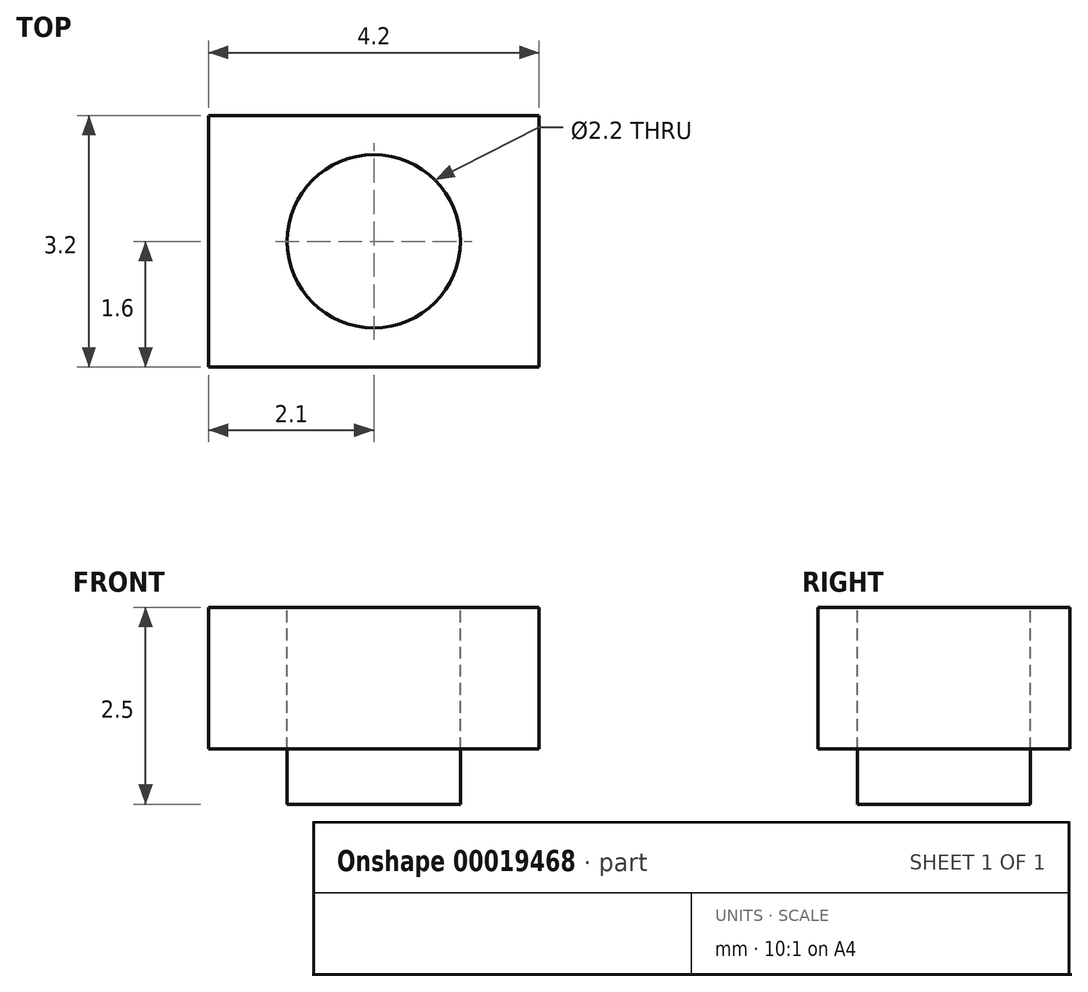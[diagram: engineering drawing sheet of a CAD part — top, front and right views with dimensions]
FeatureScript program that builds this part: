
annotation { "Feature Type Name" : "Feature", "Feature Type Description" : "" }
export const myFeature = defineFeature(function(context is Context, id is Id, definition is map)
    precondition{}
    {
        {
            var Q0;
            Q0=qCreatedBy(makeId("Top.planeOp"),FACE);
            var sketch = newSketch(context, id + "F0", { "sketchPlane" : qUnion([Q0])});
            skLineSegment(sketch, "E0.rect.bottom", {"start": v(2.1, 1.6) * mm, "end": v(-2.1, 1.6) * mm});
            skLineSegment(sketch, "E0.rect.top", {"start": v(2.1, -1.6) * mm, "end": v(-2.1, -1.6) * mm});
            skLineSegment(sketch, "E0.rect.left", {"start": v(2.1, 1.6) * mm, "end": v(2.1, -1.6) * mm});
            skLineSegment(sketch, "E0.rect.right", {"start": v(-2.1, 1.6) * mm, "end": v(-2.1, -1.6) * mm});
            skPoint(sketch, "E0.rect.middle", {"position": v(0, 0) * mm});
            skCircle(sketch, "E1", {"center": v(0, 0) * mm, "radius": 1.1 * mm});
            skSolve(sketch);
        }
        {
            var Q0;
            Q0=makeQuery(id+"F0.imprint","IMPRINT",FACE,{"disambiguationData":[TD([[makeQuery(id+"F0.imprint","IMPRINT",EDGE,{"derivedFrom":sQuery(id+"F0.wireOp",EDGE,"E0.rect.bottom")}),1.0]])]});
            extrude(context, id + "F1", {"entities" : qUnion([Q0]), "depth" : 1.8 * mm});
        }
        {
            var Q0;
            Q0=makeQuery(id+"F1.opExtrude","CAP_FACE",FACE,{"disambiguationData":[OSD([sQuery(id+"F0.wireOp",EDGE,"E0.rect.bottom"),sQuery(id+"F0.wireOp",EDGE,"E0.rect.top"),sQuery(id+"F0.wireOp",EDGE,"E0.rect.left"),sQuery(id+"F0.wireOp",EDGE,"E0.rect.right"),sQuery(id+"F0.wireOp",EDGE,"E1")])],"isStart":false});
            var sketch = newSketch(context, id + "F2", { "sketchPlane" : qUnion([Q0])});
            skCircle(sketch, "E2", {"center": v(0, 0) * mm, "radius": 1.1 * mm});
            skSolve(sketch);
        }
        {
            var Q0;
            Q0=makeQuery(id+"F2.imprint","IMPRINT",FACE,{"disambiguationData":[TD([[makeQuery(id+"F2.imprint","IMPRINT",EDGE,{"derivedFrom":sQuery(id+"F2.wireOp",EDGE,"E2")}),1.0]])]});
            extrude(context, id + "F3", {"entities" : qUnion([Q0]), "oppositeDirection" : true, "depth" : 2.5 * mm});
        }
    });
